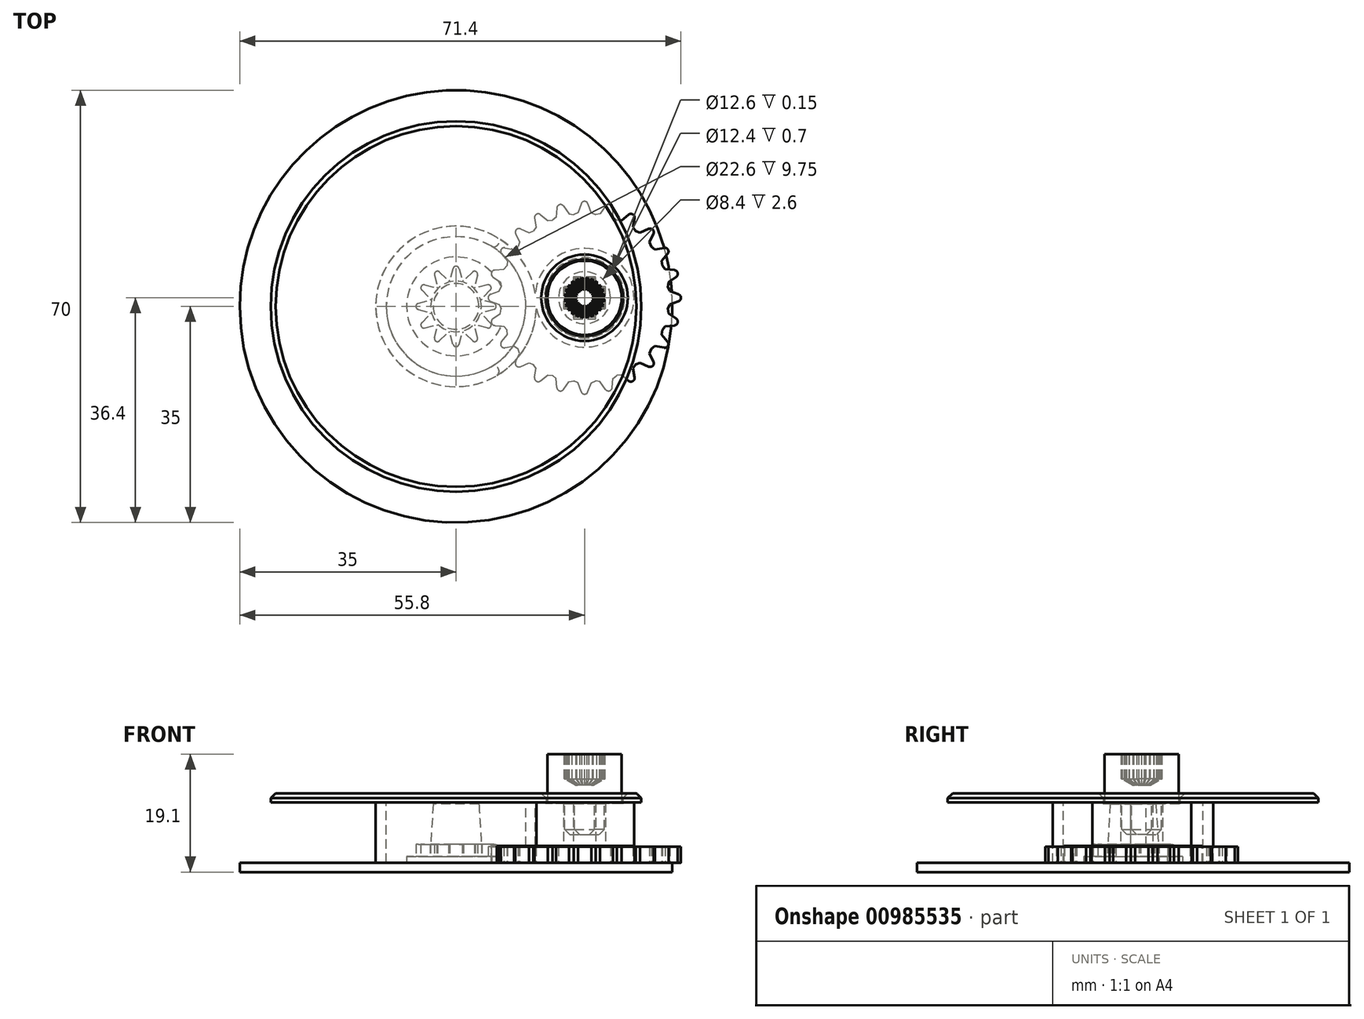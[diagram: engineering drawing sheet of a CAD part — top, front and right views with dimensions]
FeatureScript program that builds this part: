
annotation { "Feature Type Name" : "Feature", "Feature Type Description" : "" }
export const myFeature = defineFeature(function(context is Context, id is Id, definition is map)
    precondition{}
    {
        {
            var Q0;
            Q0=qCreatedBy(makeId("Front.planeOp"),FACE);
            var sketch = newSketch(context, id + "F0", { "sketchPlane" : qUnion([Q0])});
            skLineSegment(sketch, "E0", {"start": v(0, 0) * mm, "end": v(0, 9) * mm});
            skLineSegment(sketch, "E1", {"start": v(0, 9) * mm, "end": v(3.8, 9) * mm});
            skLineSegment(sketch, "E2", {"start": v(3.8, 9) * mm, "end": v(4.2, 2.5) * mm});
            skLineSegment(sketch, "E3", {"start": v(4.2, 2.5) * mm, "end": v(8, 2.5) * mm});
            skLineSegment(sketch, "E4", {"start": v(8, 2.5) * mm, "end": v(8, 1.5) * mm});
            skLineSegment(sketch, "E5", {"start": v(8, 1.5) * mm, "end": v(35, 1.5) * mm});
            skLineSegment(sketch, "E6", {"start": v(35, 1.5) * mm, "end": v(35, 0) * mm});
            skLineSegment(sketch, "E7", {"start": v(35, 0) * mm, "end": v(0, 0) * mm});
            skSolve(sketch);
        }
        {
            var Q0;
            Q0=qSketchRegion(id+"F0",true);
            var Q1;
            Q1=sQuery(id+"F0.wireOp",EDGE,"E0");
            revolve(context, id + "F1", {"surfaceOperationType" : NewSurfaceOperationType.NEW, "entities" : qUnion([Q0]), "axis" : qUnion([Q1]), "revolveType" : RevolveType.FULL});
        }
        {
            var Q0;
            Q0=qCreatedBy(makeId("Top.planeOp"),FACE);
            var sketch = newSketch(context, id + "F2", { "sketchPlane" : qUnion([Q0])});
            skCircle(sketch, "E8", {"center": v(0, 0) * mm, "radius": 15 * mm});
            skSolve(sketch);
        }
        {
            var Q0;
            Q0 = qSketchRegion(id + "F2", true);
            extrude(context, id + "F3", {"entities" : qUnion([Q0]), "depth" : 1.5 * mm, "offsetDistance" : 25 * mm});
        }
        {
            var Q0;
            Q0=makeQuery(id+"F3.opExtrude","CAP_FACE",FACE,{"disambiguationData":[OSD([sQuery(id+"F2.wireOp",EDGE,"E8")])],"isStart":false});
            var sketch = newSketch(context, id + "F4", { "sketchPlane" : qUnion([Q0])});
            skCircle(sketch, "E9", {"center": v(6, 0) * mm, "radius": 0.5 * mm});
            skLineSegment(sketch, "E10", {"start": v(6.13, 0.48) * mm, "end": v(4.2, 1) * mm});
            skLineSegment(sketch, "E11", {"start": v(4.2, 1) * mm, "end": v(3.85, 2.04) * mm});
            skLineSegment(sketch, "E12.MirrorCS", {"start": v(6.13, -0.48) * mm, "end": v(4.2, -1) * mm});
            skLineSegment(sketch, "E13.MirrorCS", {"start": v(4.2, -1) * mm, "end": v(3.85, -2.04) * mm});
            skCircle(sketch, "E14.1.0", {"center": v(5.2, 3) * mm, "radius": 0.5 * mm});
            skLineSegment(sketch, "E14.1.1", {"start": v(3.13, 2.97) * mm, "end": v(2.31, 3.69) * mm});
            skLineSegment(sketch, "E14.1.2", {"start": v(5.55, 2.65) * mm, "end": v(4.14, 1.23) * mm});
            skLineSegment(sketch, "E14.1.3", {"start": v(4.14, 1.23) * mm, "end": v(4.35, 0.16) * mm});
            skLineSegment(sketch, "E14.1.4", {"start": v(5.07, 3.48) * mm, "end": v(3.13, 2.97) * mm});
            skCircle(sketch, "E14.2.0", {"center": v(3, 5.2) * mm, "radius": 0.5 * mm});
            skLineSegment(sketch, "E14.2.1", {"start": v(1.23, 4.14) * mm, "end": v(0.16, 4.35) * mm});
            skLineSegment(sketch, "E14.2.2", {"start": v(3.48, 5.07) * mm, "end": v(2.97, 3.13) * mm});
            skLineSegment(sketch, "E14.2.3", {"start": v(2.97, 3.13) * mm, "end": v(3.69, 2.31) * mm});
            skLineSegment(sketch, "E14.2.4", {"start": v(2.65, 5.55) * mm, "end": v(1.23, 4.14) * mm});
            skCircle(sketch, "E14.3.0", {"center": v(0, 6) * mm, "radius": 0.5 * mm});
            skLineSegment(sketch, "E14.3.1", {"start": v(-1, 4.2) * mm, "end": v(-2.04, 3.85) * mm});
            skLineSegment(sketch, "E14.3.2", {"start": v(0.48, 6.13) * mm, "end": v(1, 4.2) * mm});
            skLineSegment(sketch, "E14.3.3", {"start": v(1, 4.2) * mm, "end": v(2.04, 3.85) * mm});
            skLineSegment(sketch, "E14.3.4", {"start": v(-0.48, 6.13) * mm, "end": v(-1, 4.2) * mm});
            skCircle(sketch, "E14.4.0", {"center": v(-3, 5.2) * mm, "radius": 0.5 * mm});
            skLineSegment(sketch, "E14.4.1", {"start": v(-2.97, 3.13) * mm, "end": v(-3.69, 2.31) * mm});
            skLineSegment(sketch, "E14.4.2", {"start": v(-2.65, 5.55) * mm, "end": v(-1.23, 4.14) * mm});
            skLineSegment(sketch, "E14.4.3", {"start": v(-1.23, 4.14) * mm, "end": v(-0.16, 4.35) * mm});
            skLineSegment(sketch, "E14.4.4", {"start": v(-3.48, 5.07) * mm, "end": v(-2.97, 3.13) * mm});
            skCircle(sketch, "E14.5.0", {"center": v(-5.2, 3) * mm, "radius": 0.5 * mm});
            skLineSegment(sketch, "E14.5.1", {"start": v(-4.14, 1.23) * mm, "end": v(-4.35, 0.16) * mm});
            skLineSegment(sketch, "E14.5.2", {"start": v(-5.07, 3.48) * mm, "end": v(-3.13, 2.97) * mm});
            skLineSegment(sketch, "E14.5.3", {"start": v(-3.13, 2.97) * mm, "end": v(-2.31, 3.69) * mm});
            skLineSegment(sketch, "E14.5.4", {"start": v(-5.55, 2.65) * mm, "end": v(-4.14, 1.23) * mm});
            skCircle(sketch, "E14.6.0", {"center": v(-6, 0) * mm, "radius": 0.5 * mm});
            skLineSegment(sketch, "E14.6.1", {"start": v(-4.2, -1) * mm, "end": v(-3.85, -2.04) * mm});
            skLineSegment(sketch, "E14.6.2", {"start": v(-6.13, 0.48) * mm, "end": v(-4.2, 1) * mm});
            skLineSegment(sketch, "E14.6.3", {"start": v(-4.2, 1) * mm, "end": v(-3.85, 2.04) * mm});
            skLineSegment(sketch, "E14.6.4", {"start": v(-6.13, -0.48) * mm, "end": v(-4.2, -1) * mm});
            skCircle(sketch, "E14.7.0", {"center": v(-5.2, -3) * mm, "radius": 0.5 * mm});
            skLineSegment(sketch, "E14.7.1", {"start": v(-3.13, -2.97) * mm, "end": v(-2.31, -3.69) * mm});
            skLineSegment(sketch, "E14.7.2", {"start": v(-5.55, -2.65) * mm, "end": v(-4.14, -1.23) * mm});
            skLineSegment(sketch, "E14.7.3", {"start": v(-4.14, -1.23) * mm, "end": v(-4.35, -0.16) * mm});
            skLineSegment(sketch, "E14.7.4", {"start": v(-5.07, -3.48) * mm, "end": v(-3.13, -2.97) * mm});
            skCircle(sketch, "E14.8.0", {"center": v(-3, -5.2) * mm, "radius": 0.5 * mm});
            skLineSegment(sketch, "E14.8.1", {"start": v(-1.23, -4.14) * mm, "end": v(-0.16, -4.35) * mm});
            skLineSegment(sketch, "E14.8.2", {"start": v(-3.48, -5.07) * mm, "end": v(-2.97, -3.13) * mm});
            skLineSegment(sketch, "E14.8.3", {"start": v(-2.97, -3.13) * mm, "end": v(-3.69, -2.31) * mm});
            skLineSegment(sketch, "E14.8.4", {"start": v(-2.65, -5.55) * mm, "end": v(-1.23, -4.14) * mm});
            skCircle(sketch, "E14.9.0", {"center": v(0, -6) * mm, "radius": 0.5 * mm});
            skLineSegment(sketch, "E14.9.1", {"start": v(1, -4.2) * mm, "end": v(2.04, -3.85) * mm});
            skLineSegment(sketch, "E14.9.2", {"start": v(-0.48, -6.13) * mm, "end": v(-1, -4.2) * mm});
            skLineSegment(sketch, "E14.9.3", {"start": v(-1, -4.2) * mm, "end": v(-2.04, -3.85) * mm});
            skLineSegment(sketch, "E14.9.4", {"start": v(0.48, -6.13) * mm, "end": v(1, -4.2) * mm});
            skPoint(sketch, "E14.center", {"position": v(0, 0) * mm});
            skLineSegment(sketch, "E15.2.10.0", {"start": v(2.97, -3.13) * mm, "end": v(3.69, -2.31) * mm});
            skLineSegment(sketch, "E15.5.10.0", {"start": v(2.65, -5.55) * mm, "end": v(1.23, -4.14) * mm});
            skLineSegment(sketch, "E15.8.10.0", {"start": v(1.23, -4.14) * mm, "end": v(0.16, -4.35) * mm});
            skCircle(sketch, "E15.10.10.0", {"center": v(3, -5.2) * mm, "radius": 0.5 * mm});
            skLineSegment(sketch, "E15.11.10.0", {"start": v(3.48, -5.07) * mm, "end": v(2.97, -3.13) * mm});
            skLineSegment(sketch, "E15.2.11.0", {"start": v(4.14, -1.23) * mm, "end": v(4.35, -0.16) * mm});
            skLineSegment(sketch, "E15.5.11.0", {"start": v(5.07, -3.48) * mm, "end": v(3.13, -2.97) * mm});
            skLineSegment(sketch, "E15.8.11.0", {"start": v(3.13, -2.97) * mm, "end": v(2.31, -3.69) * mm});
            skCircle(sketch, "E15.10.11.0", {"center": v(5.2, -3) * mm, "radius": 0.5 * mm});
            skLineSegment(sketch, "E15.11.11.0", {"start": v(5.55, -2.65) * mm, "end": v(4.14, -1.23) * mm});
            skSolve(sketch);
        }
        {
            var Q0;
            Q0=qSketchRegion(id+"F4",true);
            extrude(context, id + "F5", {"entities" : qUnion([Q0]), "operationType" : NewBodyOperationType.ADD, "depth" : 3 * mm, "offsetDistance" : 25 * mm});
        }
        {
            var Q0;
            Q0=makeQuery(id+"F1.opRevolve","SWEPT_FACE",FACE,{"disambiguationData":[OSD([sQuery(id+"F0.wireOp",EDGE,"E5")])]});
            var sketch = newSketch(context, id + "F6", { "sketchPlane" : qUnion([Q0])});
            skCircle(sketch, "E16", {"center": v(20.8, 1.4) * mm, "radius": 4.2 * mm});
            skCircle(sketch, "E17", {"center": v(35.8, 1.4) * mm, "radius": 0.6 * mm});
            skLineSegment(sketch, "E18", {"start": v(36, 1.96) * mm, "end": v(34.6, 2.48) * mm});
            skLineSegment(sketch, "E19", {"start": v(35.8, 1.4) * mm, "end": v(35.3, 1.4) * mm});
            skLineSegment(sketch, "E20", {"start": v(34.6, 2.48) * mm, "end": v(34.2, 3.4) * mm});
            skLineSegment(sketch, "E21.MirrorCS", {"start": v(36, 0.84) * mm, "end": v(34.6, 0.32) * mm});
            skLineSegment(sketch, "E22.MirrorCS", {"start": v(34.6, 0.32) * mm, "end": v(34.2, -0.6) * mm});
            skLineSegment(sketch, "E23.1.0", {"start": v(35.63, 4.8) * mm, "end": v(34.4, 3.93) * mm});
            skCircle(sketch, "E23.1.1", {"center": v(35.29, 5.28) * mm, "radius": 0.6 * mm});
            skLineSegment(sketch, "E23.1.2", {"start": v(35.34, 5.88) * mm, "end": v(33.85, 6.01) * mm});
            skLineSegment(sketch, "E23.1.3", {"start": v(34.4, 3.93) * mm, "end": v(34.25, 2.94) * mm});
            skLineSegment(sketch, "E23.1.4", {"start": v(33.85, 6.01) * mm, "end": v(33.22, 6.8) * mm});
            skLineSegment(sketch, "E23.1.5", {"start": v(35.29, 5.28) * mm, "end": v(34.8, 5.15) * mm});
            skLineSegment(sketch, "E23.2.0", {"start": v(34.25, 8.51) * mm, "end": v(33.29, 7.37) * mm});
            skCircle(sketch, "E23.2.1", {"center": v(33.8, 8.9) * mm, "radius": 0.6 * mm});
            skLineSegment(sketch, "E23.2.2", {"start": v(33.69, 9.5) * mm, "end": v(32.2, 9.23) * mm});
            skLineSegment(sketch, "E23.2.3", {"start": v(33.29, 7.37) * mm, "end": v(33.4, 6.37) * mm});
            skLineSegment(sketch, "E23.2.4", {"start": v(32.2, 9.23) * mm, "end": v(31.4, 9.82) * mm});
            skLineSegment(sketch, "E23.2.5", {"start": v(33.8, 8.9) * mm, "end": v(33.36, 8.65) * mm});
            skLineSegment(sketch, "E23.3.0", {"start": v(31.95, 11.75) * mm, "end": v(31.32, 10.4) * mm});
            skCircle(sketch, "E23.3.1", {"center": v(31.4, 12) * mm, "radius": 0.6 * mm});
            skLineSegment(sketch, "E23.3.2", {"start": v(31.15, 12.55) * mm, "end": v(29.8, 11.92) * mm});
            skLineSegment(sketch, "E23.3.3", {"start": v(31.32, 10.4) * mm, "end": v(31.68, 9.46) * mm});
            skLineSegment(sketch, "E23.3.4", {"start": v(29.8, 11.92) * mm, "end": v(28.86, 12.28) * mm});
            skLineSegment(sketch, "E23.3.5", {"start": v(31.4, 12) * mm, "end": v(31.05, 11.65) * mm});
            skLineSegment(sketch, "E23.4.0", {"start": v(28.9, 14.29) * mm, "end": v(28.63, 12.8) * mm});
            skCircle(sketch, "E23.4.1", {"center": v(28.3, 14.4) * mm, "radius": 0.6 * mm});
            skLineSegment(sketch, "E23.4.2", {"start": v(27.91, 14.85) * mm, "end": v(26.77, 13.89) * mm});
            skLineSegment(sketch, "E23.4.3", {"start": v(28.63, 12.8) * mm, "end": v(29.22, 12) * mm});
            skLineSegment(sketch, "E23.4.4", {"start": v(26.77, 13.89) * mm, "end": v(25.77, 14) * mm});
            skLineSegment(sketch, "E23.4.5", {"start": v(28.3, 14.4) * mm, "end": v(28.05, 13.96) * mm});
            skLineSegment(sketch, "E23.5.0", {"start": v(25.28, 15.94) * mm, "end": v(25.41, 14.45) * mm});
            skCircle(sketch, "E23.5.1", {"center": v(24.68, 15.89) * mm, "radius": 0.6 * mm});
            skLineSegment(sketch, "E23.5.2", {"start": v(24.2, 16.23) * mm, "end": v(23.33, 15) * mm});
            skLineSegment(sketch, "E23.5.3", {"start": v(25.41, 14.45) * mm, "end": v(26.2, 13.82) * mm});
            skLineSegment(sketch, "E23.5.4", {"start": v(23.33, 15) * mm, "end": v(22.34, 14.85) * mm});
            skLineSegment(sketch, "E23.5.5", {"start": v(24.68, 15.89) * mm, "end": v(24.55, 15.4) * mm});
            skLineSegment(sketch, "E23.6.0", {"start": v(21.36, 16.6) * mm, "end": v(21.88, 15.2) * mm});
            skCircle(sketch, "E23.6.1", {"center": v(20.8, 16.4) * mm, "radius": 0.6 * mm});
            skLineSegment(sketch, "E23.6.2", {"start": v(20.24, 16.6) * mm, "end": v(19.72, 15.2) * mm});
            skLineSegment(sketch, "E23.6.3", {"start": v(21.88, 15.2) * mm, "end": v(22.8, 14.8) * mm});
            skLineSegment(sketch, "E23.6.4", {"start": v(19.72, 15.2) * mm, "end": v(18.8, 14.8) * mm});
            skLineSegment(sketch, "E23.6.5", {"start": v(20.8, 16.4) * mm, "end": v(20.8, 15.9) * mm});
            skLineSegment(sketch, "E23.7.0", {"start": v(17.4, 16.23) * mm, "end": v(18.27, 15) * mm});
            skCircle(sketch, "E23.7.1", {"center": v(16.92, 15.89) * mm, "radius": 0.6 * mm});
            skLineSegment(sketch, "E23.7.2", {"start": v(16.32, 15.94) * mm, "end": v(16.19, 14.45) * mm});
            skLineSegment(sketch, "E23.7.3", {"start": v(18.27, 15) * mm, "end": v(19.26, 14.85) * mm});
            skLineSegment(sketch, "E23.7.4", {"start": v(16.19, 14.45) * mm, "end": v(15.4, 13.82) * mm});
            skLineSegment(sketch, "E23.7.5", {"start": v(16.92, 15.89) * mm, "end": v(17.05, 15.4) * mm});
            skLineSegment(sketch, "E23.8.0", {"start": v(13.69, 14.85) * mm, "end": v(14.83, 13.89) * mm});
            skCircle(sketch, "E23.8.1", {"center": v(13.3, 14.4) * mm, "radius": 0.6 * mm});
            skLineSegment(sketch, "E23.8.2", {"start": v(12.7, 14.29) * mm, "end": v(12.97, 12.8) * mm});
            skLineSegment(sketch, "E23.8.3", {"start": v(14.83, 13.89) * mm, "end": v(15.83, 14) * mm});
            skLineSegment(sketch, "E23.8.4", {"start": v(12.97, 12.8) * mm, "end": v(12.38, 12) * mm});
            skLineSegment(sketch, "E23.8.5", {"start": v(13.3, 14.4) * mm, "end": v(13.55, 13.96) * mm});
            skLineSegment(sketch, "E23.9.0", {"start": v(10.45, 12.55) * mm, "end": v(11.8, 11.92) * mm});
            skCircle(sketch, "E23.9.1", {"center": v(10.2, 12) * mm, "radius": 0.6 * mm});
            skLineSegment(sketch, "E23.9.2", {"start": v(9.65, 11.75) * mm, "end": v(10.28, 10.4) * mm});
            skLineSegment(sketch, "E23.9.3", {"start": v(11.8, 11.92) * mm, "end": v(12.74, 12.28) * mm});
            skLineSegment(sketch, "E23.9.4", {"start": v(10.28, 10.4) * mm, "end": v(9.92, 9.46) * mm});
            skLineSegment(sketch, "E23.9.5", {"start": v(10.2, 12) * mm, "end": v(10.55, 11.65) * mm});
            skLineSegment(sketch, "E23.10.0", {"start": v(7.91, 9.5) * mm, "end": v(9.4, 9.23) * mm});
            skCircle(sketch, "E23.10.1", {"center": v(7.8, 8.9) * mm, "radius": 0.6 * mm});
            skLineSegment(sketch, "E23.10.2", {"start": v(7.35, 8.51) * mm, "end": v(8.31, 7.37) * mm});
            skLineSegment(sketch, "E23.10.3", {"start": v(9.4, 9.23) * mm, "end": v(10.2, 9.82) * mm});
            skLineSegment(sketch, "E23.10.4", {"start": v(8.31, 7.37) * mm, "end": v(8.2, 6.37) * mm});
            skLineSegment(sketch, "E23.10.5", {"start": v(7.8, 8.9) * mm, "end": v(8.24, 8.65) * mm});
            skLineSegment(sketch, "E23.11.0", {"start": v(6.26, 5.88) * mm, "end": v(7.75, 6.01) * mm});
            skCircle(sketch, "E23.11.1", {"center": v(6.31, 5.28) * mm, "radius": 0.6 * mm});
            skLineSegment(sketch, "E23.11.2", {"start": v(5.97, 4.8) * mm, "end": v(7.2, 3.93) * mm});
            skLineSegment(sketch, "E23.11.3", {"start": v(7.75, 6.01) * mm, "end": v(8.38, 6.8) * mm});
            skLineSegment(sketch, "E23.11.4", {"start": v(7.2, 3.93) * mm, "end": v(7.35, 2.94) * mm});
            skLineSegment(sketch, "E23.11.5", {"start": v(6.31, 5.28) * mm, "end": v(6.8, 5.15) * mm});
            skLineSegment(sketch, "E23.12.0", {"start": v(5.6, 1.96) * mm, "end": v(7, 2.48) * mm});
            skCircle(sketch, "E23.12.1", {"center": v(5.8, 1.4) * mm, "radius": 0.6 * mm});
            skLineSegment(sketch, "E23.12.2", {"start": v(5.6, 0.84) * mm, "end": v(7, 0.32) * mm});
            skLineSegment(sketch, "E23.12.3", {"start": v(7, 2.48) * mm, "end": v(7.4, 3.4) * mm});
            skLineSegment(sketch, "E23.12.4", {"start": v(7, 0.32) * mm, "end": v(7.4, -0.6) * mm});
            skLineSegment(sketch, "E23.12.5", {"start": v(5.8, 1.4) * mm, "end": v(6.3, 1.4) * mm});
            skLineSegment(sketch, "E23.13.0", {"start": v(5.97, -2) * mm, "end": v(7.2, -1.13) * mm});
            skCircle(sketch, "E23.13.1", {"center": v(6.31, -2.48) * mm, "radius": 0.6 * mm});
            skLineSegment(sketch, "E23.13.2", {"start": v(6.26, -3.08) * mm, "end": v(7.75, -3.21) * mm});
            skLineSegment(sketch, "E23.13.3", {"start": v(7.2, -1.13) * mm, "end": v(7.35, -0.14) * mm});
            skLineSegment(sketch, "E23.13.4", {"start": v(7.75, -3.21) * mm, "end": v(8.38, -4) * mm});
            skLineSegment(sketch, "E23.13.5", {"start": v(6.31, -2.48) * mm, "end": v(6.8, -2.35) * mm});
            skLineSegment(sketch, "E23.14.0", {"start": v(7.35, -5.71) * mm, "end": v(8.31, -4.57) * mm});
            skCircle(sketch, "E23.14.1", {"center": v(7.8, -6.1) * mm, "radius": 0.6 * mm});
            skLineSegment(sketch, "E23.14.2", {"start": v(7.91, -6.7) * mm, "end": v(9.4, -6.43) * mm});
            skLineSegment(sketch, "E23.14.3", {"start": v(8.31, -4.57) * mm, "end": v(8.2, -3.57) * mm});
            skLineSegment(sketch, "E23.14.4", {"start": v(9.4, -6.43) * mm, "end": v(10.2, -7.02) * mm});
            skLineSegment(sketch, "E23.14.5", {"start": v(7.8, -6.1) * mm, "end": v(8.24, -5.85) * mm});
            skLineSegment(sketch, "E23.15.0", {"start": v(9.65, -8.95) * mm, "end": v(10.28, -7.6) * mm});
            skCircle(sketch, "E23.15.1", {"center": v(10.2, -9.2) * mm, "radius": 0.6 * mm});
            skLineSegment(sketch, "E23.15.2", {"start": v(10.45, -9.75) * mm, "end": v(11.8, -9.12) * mm});
            skLineSegment(sketch, "E23.15.3", {"start": v(10.28, -7.6) * mm, "end": v(9.92, -6.66) * mm});
            skLineSegment(sketch, "E23.15.4", {"start": v(11.8, -9.12) * mm, "end": v(12.74, -9.48) * mm});
            skLineSegment(sketch, "E23.15.5", {"start": v(10.2, -9.2) * mm, "end": v(10.55, -8.85) * mm});
            skLineSegment(sketch, "E23.16.0", {"start": v(12.7, -11.49) * mm, "end": v(12.97, -10) * mm});
            skCircle(sketch, "E23.16.1", {"center": v(13.3, -11.6) * mm, "radius": 0.6 * mm});
            skLineSegment(sketch, "E23.16.2", {"start": v(13.69, -12.05) * mm, "end": v(14.83, -11.09) * mm});
            skLineSegment(sketch, "E23.16.3", {"start": v(12.97, -10) * mm, "end": v(12.38, -9.2) * mm});
            skLineSegment(sketch, "E23.16.4", {"start": v(14.83, -11.09) * mm, "end": v(15.83, -11.2) * mm});
            skLineSegment(sketch, "E23.16.5", {"start": v(13.3, -11.6) * mm, "end": v(13.55, -11.16) * mm});
            skLineSegment(sketch, "E23.17.0", {"start": v(16.32, -13.14) * mm, "end": v(16.19, -11.65) * mm});
            skCircle(sketch, "E23.17.1", {"center": v(16.92, -13.09) * mm, "radius": 0.6 * mm});
            skLineSegment(sketch, "E23.17.2", {"start": v(17.4, -13.43) * mm, "end": v(18.27, -12.2) * mm});
            skLineSegment(sketch, "E23.17.3", {"start": v(16.19, -11.65) * mm, "end": v(15.4, -11.02) * mm});
            skLineSegment(sketch, "E23.17.4", {"start": v(18.27, -12.2) * mm, "end": v(19.26, -12.05) * mm});
            skLineSegment(sketch, "E23.17.5", {"start": v(16.92, -13.09) * mm, "end": v(17.05, -12.6) * mm});
            skLineSegment(sketch, "E23.18.0", {"start": v(20.24, -13.8) * mm, "end": v(19.72, -12.4) * mm});
            skCircle(sketch, "E23.18.1", {"center": v(20.8, -13.6) * mm, "radius": 0.6 * mm});
            skLineSegment(sketch, "E23.18.2", {"start": v(21.36, -13.8) * mm, "end": v(21.88, -12.4) * mm});
            skLineSegment(sketch, "E23.18.3", {"start": v(19.72, -12.4) * mm, "end": v(18.8, -12) * mm});
            skLineSegment(sketch, "E23.18.4", {"start": v(21.88, -12.4) * mm, "end": v(22.8, -12) * mm});
            skLineSegment(sketch, "E23.18.5", {"start": v(20.8, -13.6) * mm, "end": v(20.8, -13.1) * mm});
            skLineSegment(sketch, "E23.19.0", {"start": v(24.2, -13.43) * mm, "end": v(23.33, -12.2) * mm});
            skCircle(sketch, "E23.19.1", {"center": v(24.68, -13.09) * mm, "radius": 0.6 * mm});
            skLineSegment(sketch, "E23.19.2", {"start": v(25.28, -13.14) * mm, "end": v(25.41, -11.65) * mm});
            skLineSegment(sketch, "E23.19.3", {"start": v(23.33, -12.2) * mm, "end": v(22.34, -12.05) * mm});
            skLineSegment(sketch, "E23.19.4", {"start": v(25.41, -11.65) * mm, "end": v(26.2, -11.02) * mm});
            skLineSegment(sketch, "E23.19.5", {"start": v(24.68, -13.09) * mm, "end": v(24.55, -12.6) * mm});
            skLineSegment(sketch, "E23.20.0", {"start": v(27.91, -12.05) * mm, "end": v(26.77, -11.09) * mm});
            skCircle(sketch, "E23.20.1", {"center": v(28.3, -11.6) * mm, "radius": 0.6 * mm});
            skLineSegment(sketch, "E23.20.2", {"start": v(28.9, -11.49) * mm, "end": v(28.63, -10) * mm});
            skLineSegment(sketch, "E23.20.3", {"start": v(26.77, -11.09) * mm, "end": v(25.77, -11.2) * mm});
            skLineSegment(sketch, "E23.20.4", {"start": v(28.63, -10) * mm, "end": v(29.22, -9.2) * mm});
            skLineSegment(sketch, "E23.20.5", {"start": v(28.3, -11.6) * mm, "end": v(28.05, -11.16) * mm});
            skLineSegment(sketch, "E23.21.0", {"start": v(31.15, -9.75) * mm, "end": v(29.8, -9.12) * mm});
            skCircle(sketch, "E23.21.1", {"center": v(31.4, -9.2) * mm, "radius": 0.6 * mm});
            skLineSegment(sketch, "E23.21.2", {"start": v(31.95, -8.95) * mm, "end": v(31.32, -7.6) * mm});
            skLineSegment(sketch, "E23.21.3", {"start": v(29.8, -9.12) * mm, "end": v(28.86, -9.48) * mm});
            skLineSegment(sketch, "E23.21.4", {"start": v(31.32, -7.6) * mm, "end": v(31.68, -6.66) * mm});
            skLineSegment(sketch, "E23.21.5", {"start": v(31.4, -9.2) * mm, "end": v(31.05, -8.85) * mm});
            skLineSegment(sketch, "E23.22.0", {"start": v(33.69, -6.7) * mm, "end": v(32.2, -6.43) * mm});
            skCircle(sketch, "E23.22.1", {"center": v(33.8, -6.1) * mm, "radius": 0.6 * mm});
            skLineSegment(sketch, "E23.22.2", {"start": v(34.25, -5.71) * mm, "end": v(33.29, -4.57) * mm});
            skLineSegment(sketch, "E23.22.3", {"start": v(32.2, -6.43) * mm, "end": v(31.4, -7.02) * mm});
            skLineSegment(sketch, "E23.22.4", {"start": v(33.29, -4.57) * mm, "end": v(33.4, -3.57) * mm});
            skLineSegment(sketch, "E23.22.5", {"start": v(33.8, -6.1) * mm, "end": v(33.36, -5.85) * mm});
            skLineSegment(sketch, "E23.23.0", {"start": v(35.34, -3.08) * mm, "end": v(33.85, -3.21) * mm});
            skCircle(sketch, "E23.23.1", {"center": v(35.29, -2.48) * mm, "radius": 0.6 * mm});
            skLineSegment(sketch, "E23.23.2", {"start": v(35.63, -2) * mm, "end": v(34.4, -1.13) * mm});
            skLineSegment(sketch, "E23.23.3", {"start": v(33.85, -3.21) * mm, "end": v(33.22, -4) * mm});
            skLineSegment(sketch, "E23.23.4", {"start": v(34.4, -1.13) * mm, "end": v(34.25, -0.14) * mm});
            skLineSegment(sketch, "E23.23.5", {"start": v(35.29, -2.48) * mm, "end": v(34.8, -2.35) * mm});
            skSolve(sketch);
        }
        {
            var Q0;
            Q0 = qSketchRegion(id + "F6", true);
            extrude(context, id + "F7", {"entities" : qUnion([Q0]), "depth" : 2.6 * mm, "offsetDistance" : 25 * mm});
        }
        {
            var Q0;
            Q0=makeQuery(id+"F5.opExtrude","CAP_FACE",FACE,{"disambiguationData":[OSD([sQuery(id+"F4.wireOp",EDGE,"0EXkI3EO-WUdj-fHIo-xL43-ZjD347GY3SOE"),sQuery(id+"F4.wireOp",EDGE,"E9"),sQuery(id+"F4.wireOp",EDGE,"E10"),sQuery(id+"F4.wireOp",EDGE,"E11"),sQuery(id+"F4.wireOp",EDGE,"E12.MirrorCS"),sQuery(id+"F4.wireOp",EDGE,"E13.MirrorCS"),sQuery(id+"F4.wireOp",EDGE,"E14.1.0"),sQuery(id+"F4.wireOp",EDGE,"E14.1.1"),sQuery(id+"F4.wireOp",EDGE,"E14.1.2"),sQuery(id+"F4.wireOp",EDGE,"E14.1.3"),sQuery(id+"F4.wireOp",EDGE,"E14.1.4"),sQuery(id+"F4.wireOp",EDGE,"E14.2.0"),sQuery(id+"F4.wireOp",EDGE,"E14.2.1"),sQuery(id+"F4.wireOp",EDGE,"E14.2.2"),sQuery(id+"F4.wireOp",EDGE,"E14.2.3"),sQuery(id+"F4.wireOp",EDGE,"E14.2.4"),sQuery(id+"F4.wireOp",EDGE,"E14.3.0"),sQuery(id+"F4.wireOp",EDGE,"E14.3.1"),sQuery(id+"F4.wireOp",EDGE,"E14.3.2"),sQuery(id+"F4.wireOp",EDGE,"E14.3.3"),sQuery(id+"F4.wireOp",EDGE,"E14.3.4"),sQuery(id+"F4.wireOp",EDGE,"E14.4.0"),sQuery(id+"F4.wireOp",EDGE,"E14.4.1"),sQuery(id+"F4.wireOp",EDGE,"E14.4.2"),sQuery(id+"F4.wireOp",EDGE,"E14.4.3"),sQuery(id+"F4.wireOp",EDGE,"E14.4.4"),sQuery(id+"F4.wireOp",EDGE,"E14.5.0"),sQuery(id+"F4.wireOp",EDGE,"E14.5.1"),sQuery(id+"F4.wireOp",EDGE,"E14.5.2"),sQuery(id+"F4.wireOp",EDGE,"E14.5.3"),sQuery(id+"F4.wireOp",EDGE,"E14.5.4"),sQuery(id+"F4.wireOp",EDGE,"E14.6.0"),sQuery(id+"F4.wireOp",EDGE,"E14.6.1"),sQuery(id+"F4.wireOp",EDGE,"E14.6.2"),sQuery(id+"F4.wireOp",EDGE,"E14.6.3"),sQuery(id+"F4.wireOp",EDGE,"E14.6.4"),sQuery(id+"F4.wireOp",EDGE,"E14.7.0"),sQuery(id+"F4.wireOp",EDGE,"E14.7.1"),sQuery(id+"F4.wireOp",EDGE,"E14.7.2"),sQuery(id+"F4.wireOp",EDGE,"E14.7.3"),sQuery(id+"F4.wireOp",EDGE,"E14.7.4"),sQuery(id+"F4.wireOp",EDGE,"E14.8.0"),sQuery(id+"F4.wireOp",EDGE,"E14.8.1"),sQuery(id+"F4.wireOp",EDGE,"E14.8.2"),sQuery(id+"F4.wireOp",EDGE,"E14.8.3"),sQuery(id+"F4.wireOp",EDGE,"E14.8.4"),sQuery(id+"F4.wireOp",EDGE,"E14.9.0"),sQuery(id+"F4.wireOp",EDGE,"E14.9.1"),sQuery(id+"F4.wireOp",EDGE,"E14.9.2"),sQuery(id+"F4.wireOp",EDGE,"E14.9.3"),sQuery(id+"F4.wireOp",EDGE,"E14.9.4"),sQuery(id+"F4.wireOp",EDGE,"E15.2.10.0"),sQuery(id+"F4.wireOp",EDGE,"E15.5.10.0"),sQuery(id+"F4.wireOp",EDGE,"E15.8.10.0"),sQuery(id+"F4.wireOp",EDGE,"E15.10.10.0"),sQuery(id+"F4.wireOp",EDGE,"E15.11.10.0"),sQuery(id+"F4.wireOp",EDGE,"E15.2.11.0"),sQuery(id+"F4.wireOp",EDGE,"E15.5.11.0"),sQuery(id+"F4.wireOp",EDGE,"E15.8.11.0"),sQuery(id+"F4.wireOp",EDGE,"E15.10.11.0"),sQuery(id+"F4.wireOp",EDGE,"E15.11.11.0")])],"isStart":false});
            var sketch = newSketch(context, id + "F8", { "sketchPlane" : qUnion([Q0])});
            skSolve(sketch);
        }
        {
            var Q0;
            Q0=makeQuery(id+"F8.imprint","IMPRINT",FACE,{"disambiguationData":[TD([[makeQuery(id+"F8.imprint","IMPRINT",EDGE,{"derivedFrom":makeQuery(id+"F5.opExtrude","CAP_EDGE",EDGE,{"disambiguationData":[OSD([sQuery(id+"F4.wireOp",EDGE,"E9")])],"isStart":false})}),1.0]])]});
            var sketch = newSketch(context, id + "F9", { "sketchPlane" : qUnion([Q0])});
            skCircle(sketch, "E24", {"center": v(0, 0) * mm, "radius": 4.1 * mm});
            skSolve(sketch);
        }
        {
            var Q0;
            Q0 = qSketchRegion(id + "F9", true);
            extrude(context, id + "F10", {"entities" : qUnion([Q0]), "operationType" : NewBodyOperationType.ADD, "depth" : 6.5 * mm, "offsetDistance" : 25 * mm});
        }
        {
            var Q0;
            Q0=makeQuery(id+"F10.opExtrude","CAP_EDGE",EDGE,{"disambiguationData":[OSD([sQuery(id+"F9.wireOp",EDGE,"E24")])],"isStart":false});
            chamfer(context, id + "F11", {"entities" : qUnion([Q0]), "chamferType" : ChamferType.TWO_OFFSETS, "width1" : .4 * mm, "oppositeDirection" : false, "width2" : 6.5 * mm, "tangentPropagation" : true});
        }
        {
            var Q0;
            Q0=makeQuery(id+"F10.opExtrude","CAP_FACE",FACE,{"disambiguationData":[OSD([sQuery(id+"F9.wireOp",EDGE,"E24")])],"isStart":false});
            cPlane(context, id + "F12", {"entities" : qUnion([Q0]), "cplaneType" : CPlaneType.OFFSET, "offset" : .25 * mm, "width" : 150 * mm, "height" : 150 * mm});
        }
        {
            var Q0;
            Q0=qCreatedBy(id+"F12.planeOp",FACE);
            var sketch = newSketch(context, id + "F13", { "sketchPlane" : qUnion([Q0])});
            skCircle(sketch, "E25", {"center": v(0, 0) * mm, "radius": 30 * mm});
            skCircle(sketch, "E26", {"center": v(20.8, 1.4) * mm, "radius": 6.2 * mm});
            skSolve(sketch);
        }
        {
            var Q0;
            Q0 = qSketchRegion(id + "F13", true);
            extrude(context, id + "F14", {"entities" : qUnion([Q0]), "depth" : 1.5 * mm, "offsetDistance" : 25 * mm});
        }
        {
            var Q0;
            Q0=makeQuery(id+"F14.opExtrude","CAP_FACE",FACE,{"disambiguationData":[OSD([sQuery(id+"F13.wireOp",EDGE,"E25")])],"isStart":true});
            var sketch = newSketch(context, id + "F15", { "sketchPlane" : qUnion([Q0])});
            skCircle(sketch, "E27", {"center": v(0, 0) * mm, "radius": 11.3 * mm});
            skCircle(sketch, "E28", {"center": v(0, 0) * mm, "radius": 13 * mm});
            skCircle(sketch, "E29", {"center": v(20.8, -1.4) * mm, "radius": 6.3 * mm});
            skCircle(sketch, "E30", {"center": v(20.8, -1.4) * mm, "radius": 8 * mm});
            skSolve(sketch);
        }
        {
            var Q0;
            Q0 = qSketchRegion(id + "F15", true);
            extrude(context, id + "F16", {"entities" : qUnion([Q0]), "operationType" : NewBodyOperationType.ADD, "depth" : 7 * mm, "offsetDistance" : 25 * mm});
        }
        {
            var Q0;
            Q0=makeQuery(id+"F7.opExtrude","CAP_FACE",FACE,{"disambiguationData":[OSD([sQuery(id+"F6.wireOp",EDGE,"E16"),sQuery(id+"F6.wireOp",EDGE,"E17"),sQuery(id+"F6.wireOp",EDGE,"E18"),sQuery(id+"F6.wireOp",EDGE,"E20"),sQuery(id+"F6.wireOp",EDGE,"E21.MirrorCS"),sQuery(id+"F6.wireOp",EDGE,"E22.MirrorCS"),sQuery(id+"F6.wireOp",EDGE,"E23.1.0"),sQuery(id+"F6.wireOp",EDGE,"E23.1.1"),sQuery(id+"F6.wireOp",EDGE,"E23.1.2"),sQuery(id+"F6.wireOp",EDGE,"E23.1.3"),sQuery(id+"F6.wireOp",EDGE,"E23.1.4"),sQuery(id+"F6.wireOp",EDGE,"E23.2.0"),sQuery(id+"F6.wireOp",EDGE,"E23.2.1"),sQuery(id+"F6.wireOp",EDGE,"E23.2.2"),sQuery(id+"F6.wireOp",EDGE,"E23.2.3"),sQuery(id+"F6.wireOp",EDGE,"E23.2.4"),sQuery(id+"F6.wireOp",EDGE,"E23.3.0"),sQuery(id+"F6.wireOp",EDGE,"E23.3.1"),sQuery(id+"F6.wireOp",EDGE,"E23.3.2"),sQuery(id+"F6.wireOp",EDGE,"E23.3.3"),sQuery(id+"F6.wireOp",EDGE,"E23.3.4"),sQuery(id+"F6.wireOp",EDGE,"E23.4.0"),sQuery(id+"F6.wireOp",EDGE,"E23.4.1"),sQuery(id+"F6.wireOp",EDGE,"E23.4.2"),sQuery(id+"F6.wireOp",EDGE,"E23.4.3"),sQuery(id+"F6.wireOp",EDGE,"E23.4.4"),sQuery(id+"F6.wireOp",EDGE,"E23.5.0"),sQuery(id+"F6.wireOp",EDGE,"E23.5.1"),sQuery(id+"F6.wireOp",EDGE,"E23.5.2"),sQuery(id+"F6.wireOp",EDGE,"E23.5.3"),sQuery(id+"F6.wireOp",EDGE,"E23.5.4"),sQuery(id+"F6.wireOp",EDGE,"E23.6.0"),sQuery(id+"F6.wireOp",EDGE,"E23.6.1"),sQuery(id+"F6.wireOp",EDGE,"E23.6.2"),sQuery(id+"F6.wireOp",EDGE,"E23.6.3"),sQuery(id+"F6.wireOp",EDGE,"E23.6.4"),sQuery(id+"F6.wireOp",EDGE,"E23.7.0"),sQuery(id+"F6.wireOp",EDGE,"E23.7.1"),sQuery(id+"F6.wireOp",EDGE,"E23.7.2"),sQuery(id+"F6.wireOp",EDGE,"E23.7.3"),sQuery(id+"F6.wireOp",EDGE,"E23.7.4"),sQuery(id+"F6.wireOp",EDGE,"E23.8.0"),sQuery(id+"F6.wireOp",EDGE,"E23.8.1"),sQuery(id+"F6.wireOp",EDGE,"E23.8.2"),sQuery(id+"F6.wireOp",EDGE,"E23.8.3"),sQuery(id+"F6.wireOp",EDGE,"E23.8.4"),sQuery(id+"F6.wireOp",EDGE,"E23.9.0"),sQuery(id+"F6.wireOp",EDGE,"E23.9.1"),sQuery(id+"F6.wireOp",EDGE,"E23.9.2"),sQuery(id+"F6.wireOp",EDGE,"E23.9.3"),sQuery(id+"F6.wireOp",EDGE,"E23.9.4"),sQuery(id+"F6.wireOp",EDGE,"E23.10.0"),sQuery(id+"F6.wireOp",EDGE,"E23.10.1"),sQuery(id+"F6.wireOp",EDGE,"E23.10.2"),sQuery(id+"F6.wireOp",EDGE,"E23.10.3"),sQuery(id+"F6.wireOp",EDGE,"E23.10.4"),sQuery(id+"F6.wireOp",EDGE,"E23.11.0"),sQuery(id+"F6.wireOp",EDGE,"E23.11.1"),sQuery(id+"F6.wireOp",EDGE,"E23.11.2"),sQuery(id+"F6.wireOp",EDGE,"E23.11.3"),sQuery(id+"F6.wireOp",EDGE,"E23.11.4"),sQuery(id+"F6.wireOp",EDGE,"E23.12.0"),sQuery(id+"F6.wireOp",EDGE,"E23.12.1"),sQuery(id+"F6.wireOp",EDGE,"E23.12.2"),sQuery(id+"F6.wireOp",EDGE,"E23.12.3"),sQuery(id+"F6.wireOp",EDGE,"E23.12.4"),sQuery(id+"F6.wireOp",EDGE,"E23.13.0"),sQuery(id+"F6.wireOp",EDGE,"E23.13.1"),sQuery(id+"F6.wireOp",EDGE,"E23.13.2"),sQuery(id+"F6.wireOp",EDGE,"E23.13.3"),sQuery(id+"F6.wireOp",EDGE,"E23.13.4"),sQuery(id+"F6.wireOp",EDGE,"E23.14.0"),sQuery(id+"F6.wireOp",EDGE,"E23.14.1"),sQuery(id+"F6.wireOp",EDGE,"E23.14.2"),sQuery(id+"F6.wireOp",EDGE,"E23.14.3"),sQuery(id+"F6.wireOp",EDGE,"E23.14.4"),sQuery(id+"F6.wireOp",EDGE,"E23.15.0"),sQuery(id+"F6.wireOp",EDGE,"E23.15.1"),sQuery(id+"F6.wireOp",EDGE,"E23.15.2"),sQuery(id+"F6.wireOp",EDGE,"E23.15.3"),sQuery(id+"F6.wireOp",EDGE,"E23.15.4"),sQuery(id+"F6.wireOp",EDGE,"E23.16.0"),sQuery(id+"F6.wireOp",EDGE,"E23.16.1"),sQuery(id+"F6.wireOp",EDGE,"E23.16.2"),sQuery(id+"F6.wireOp",EDGE,"E23.16.3"),sQuery(id+"F6.wireOp",EDGE,"E23.16.4"),sQuery(id+"F6.wireOp",EDGE,"E23.17.0"),sQuery(id+"F6.wireOp",EDGE,"E23.17.1"),sQuery(id+"F6.wireOp",EDGE,"E23.17.2"),sQuery(id+"F6.wireOp",EDGE,"E23.17.3"),sQuery(id+"F6.wireOp",EDGE,"E23.17.4"),sQuery(id+"F6.wireOp",EDGE,"E23.18.0"),sQuery(id+"F6.wireOp",EDGE,"E23.18.1"),sQuery(id+"F6.wireOp",EDGE,"E23.18.2"),sQuery(id+"F6.wireOp",EDGE,"E23.18.3"),sQuery(id+"F6.wireOp",EDGE,"E23.18.4"),sQuery(id+"F6.wireOp",EDGE,"E23.19.0"),sQuery(id+"F6.wireOp",EDGE,"E23.19.1"),sQuery(id+"F6.wireOp",EDGE,"E23.19.2"),sQuery(id+"F6.wireOp",EDGE,"E23.19.3"),sQuery(id+"F6.wireOp",EDGE,"E23.19.4"),sQuery(id+"F6.wireOp",EDGE,"E23.20.0"),sQuery(id+"F6.wireOp",EDGE,"E23.20.1"),sQuery(id+"F6.wireOp",EDGE,"E23.20.2"),sQuery(id+"F6.wireOp",EDGE,"E23.20.3"),sQuery(id+"F6.wireOp",EDGE,"E23.20.4"),sQuery(id+"F6.wireOp",EDGE,"E23.21.0"),sQuery(id+"F6.wireOp",EDGE,"E23.21.1"),sQuery(id+"F6.wireOp",EDGE,"E23.21.2"),sQuery(id+"F6.wireOp",EDGE,"E23.21.3"),sQuery(id+"F6.wireOp",EDGE,"E23.21.4"),sQuery(id+"F6.wireOp",EDGE,"E23.22.0"),sQuery(id+"F6.wireOp",EDGE,"E23.22.1"),sQuery(id+"F6.wireOp",EDGE,"E23.22.2"),sQuery(id+"F6.wireOp",EDGE,"E23.22.3"),sQuery(id+"F6.wireOp",EDGE,"E23.22.4"),sQuery(id+"F6.wireOp",EDGE,"E23.23.0"),sQuery(id+"F6.wireOp",EDGE,"E23.23.1"),sQuery(id+"F6.wireOp",EDGE,"E23.23.2"),sQuery(id+"F6.wireOp",EDGE,"E23.23.3"),sQuery(id+"F6.wireOp",EDGE,"E23.23.4")])],"isStart":false});
            var sketch = newSketch(context, id + "F17", { "sketchPlane" : qUnion([Q0])});
            skCircle(sketch, "E31", {"center": v(20.8, 1.4) * mm, "radius": 6.5 * mm});
            skLineSegment(sketch, "E32", {"start": v(24.2, 1.4) * mm, "end": v(24.2, 3.2) * mm});
            skLineSegment(sketch, "E33", {"start": v(24.2, 3.2) * mm, "end": v(22.6, 3.2) * mm});
            skLineSegment(sketch, "E34", {"start": v(22.6, 3.2) * mm, "end": v(22.6, 4.8) * mm});
            skLineSegment(sketch, "E35", {"start": v(22.6, 4.8) * mm, "end": v(20.8, 4.8) * mm});
            skLineSegment(sketch, "E36", {"start": v(20.8, 4.8) * mm, "end": v(20.8, 1.4) * mm});
            skLineSegment(sketch, "E37", {"start": v(24.2, 1.4) * mm, "end": v(20.8, 1.4) * mm});
            skLineSegment(sketch, "E38.1.0", {"start": v(17.4, 1.4) * mm, "end": v(20.8, 1.4) * mm});
            skLineSegment(sketch, "E38.1.1", {"start": v(20.8, 4.8) * mm, "end": v(19, 4.8) * mm});
            skLineSegment(sketch, "E38.1.3", {"start": v(19, 4.8) * mm, "end": v(19, 3.2) * mm});
            skLineSegment(sketch, "E38.1.4", {"start": v(19, 3.2) * mm, "end": v(17.4, 3.2) * mm});
            skLineSegment(sketch, "E38.1.5", {"start": v(17.4, 3.2) * mm, "end": v(17.4, 1.4) * mm});
            skLineSegment(sketch, "E38.2.0", {"start": v(20.8, -2) * mm, "end": v(20.8, 1.4) * mm});
            skLineSegment(sketch, "E38.2.1", {"start": v(17.4, 1.4) * mm, "end": v(17.4, -0.4) * mm});
            skLineSegment(sketch, "E38.2.2", {"start": v(17.4, 1.4) * mm, "end": v(20.8, 1.4) * mm});
            skLineSegment(sketch, "E38.2.3", {"start": v(17.4, -0.4) * mm, "end": v(19, -0.4) * mm});
            skLineSegment(sketch, "E38.2.4", {"start": v(19, -0.4) * mm, "end": v(19, -2) * mm});
            skLineSegment(sketch, "E38.2.5", {"start": v(19, -2) * mm, "end": v(20.8, -2) * mm});
            skLineSegment(sketch, "E38.3.1", {"start": v(20.8, -2) * mm, "end": v(22.6, -2) * mm});
            skLineSegment(sketch, "E38.3.2", {"start": v(20.8, -2) * mm, "end": v(20.8, 1.4) * mm});
            skLineSegment(sketch, "E38.3.3", {"start": v(22.6, -2) * mm, "end": v(22.6, -0.4) * mm});
            skLineSegment(sketch, "E38.3.4", {"start": v(22.6, -0.4) * mm, "end": v(24.2, -0.4) * mm});
            skLineSegment(sketch, "E38.3.5", {"start": v(24.2, -0.4) * mm, "end": v(24.2, 1.4) * mm});
            skSolve(sketch);
        }
        {
            var Q0;
            Q0 = qSketchRegion(id + "F17", true);
            extrude(context, id + "F18", {"entities" : qUnion([Q0]), "operationType" : NewBodyOperationType.ADD, "depth" : 7 * mm, "offsetDistance" : 25 * mm});
        }
        {
            var Q0;
            Q0=makeQuery(id+"F18.opExtrude","CAP_FACE",FACE,{"disambiguationData":[OSD([sQuery(id+"F17.wireOp",EDGE,"E31"),sQuery(id+"F17.wireOp",EDGE,"E32"),sQuery(id+"F17.wireOp",EDGE,"E33"),sQuery(id+"F17.wireOp",EDGE,"E34"),sQuery(id+"F17.wireOp",EDGE,"E35"),sQuery(id+"F17.wireOp",EDGE,"E38.1.1"),sQuery(id+"F17.wireOp",EDGE,"E38.1.3"),sQuery(id+"F17.wireOp",EDGE,"E38.1.4"),sQuery(id+"F17.wireOp",EDGE,"E38.1.5"),sQuery(id+"F17.wireOp",EDGE,"E38.2.1"),sQuery(id+"F17.wireOp",EDGE,"E38.2.3"),sQuery(id+"F17.wireOp",EDGE,"E38.2.4"),sQuery(id+"F17.wireOp",EDGE,"E38.2.5"),sQuery(id+"F17.wireOp",EDGE,"E38.3.1"),sQuery(id+"F17.wireOp",EDGE,"E38.3.3"),sQuery(id+"F17.wireOp",EDGE,"E38.3.4"),sQuery(id+"F17.wireOp",EDGE,"E38.3.5")])],"isStart":false});
            var sketch = newSketch(context, id + "F19", { "sketchPlane" : qUnion([Q0])});
            skLineSegment(sketch, "E39", {"start": v(20.8, 1.4) * mm, "end": v(20.8, 4.6) * mm});
            skLineSegment(sketch, "E40", {"start": v(20.8, 4.6) * mm, "end": v(22.4, 4.6) * mm});
            skLineSegment(sketch, "E41", {"start": v(22.4, 4.6) * mm, "end": v(22.4, 3) * mm});
            skLineSegment(sketch, "E42", {"start": v(22.4, 3) * mm, "end": v(24, 3) * mm});
            skLineSegment(sketch, "E43", {"start": v(24, 3) * mm, "end": v(24, 1.4) * mm});
            skLineSegment(sketch, "E44", {"start": v(24, 1.4) * mm, "end": v(20.8, 1.4) * mm});
            skLineSegment(sketch, "E45.1.0", {"start": v(17.6, 1.4) * mm, "end": v(17.6, 3) * mm});
            skLineSegment(sketch, "E45.1.1", {"start": v(20.8, 4.6) * mm, "end": v(20.8, 1.4) * mm});
            skLineSegment(sketch, "E45.1.2", {"start": v(20.8, 1.4) * mm, "end": v(17.6, 1.4) * mm});
            skLineSegment(sketch, "E45.1.3", {"start": v(19.2, 3) * mm, "end": v(19.2, 4.6) * mm});
            skLineSegment(sketch, "E45.1.4", {"start": v(19.2, 4.6) * mm, "end": v(20.8, 4.6) * mm});
            skLineSegment(sketch, "E45.1.5", {"start": v(17.6, 3) * mm, "end": v(19.2, 3) * mm});
            skLineSegment(sketch, "E45.2.0", {"start": v(20.8, -1.8) * mm, "end": v(19.2, -1.8) * mm});
            skLineSegment(sketch, "E45.2.1", {"start": v(17.6, 1.4) * mm, "end": v(20.8, 1.4) * mm});
            skLineSegment(sketch, "E45.2.2", {"start": v(20.8, 1.4) * mm, "end": v(20.8, -1.8) * mm});
            skLineSegment(sketch, "E45.2.3", {"start": v(19.2, -0.2) * mm, "end": v(17.6, -0.2) * mm});
            skLineSegment(sketch, "E45.2.4", {"start": v(17.6, -0.2) * mm, "end": v(17.6, 1.4) * mm});
            skLineSegment(sketch, "E45.2.5", {"start": v(19.2, -1.8) * mm, "end": v(19.2, -0.2) * mm});
            skLineSegment(sketch, "E45.3.0", {"start": v(24, 1.4) * mm, "end": v(24, -0.2) * mm});
            skLineSegment(sketch, "E45.3.1", {"start": v(20.8, -1.8) * mm, "end": v(20.8, 1.4) * mm});
            skLineSegment(sketch, "E45.3.2", {"start": v(20.8, 1.4) * mm, "end": v(24, 1.4) * mm});
            skLineSegment(sketch, "E45.3.3", {"start": v(22.4, -0.2) * mm, "end": v(22.4, -1.8) * mm});
            skLineSegment(sketch, "E45.3.4", {"start": v(22.4, -1.8) * mm, "end": v(20.8, -1.8) * mm});
            skLineSegment(sketch, "E45.3.5", {"start": v(24, -0.2) * mm, "end": v(22.4, -0.2) * mm});
            skPoint(sketch, "E45.center", {"position": v(20.8, 1.4) * mm});
            skSolve(sketch);
        }
        {
            var Q0;
            Q0 = qSketchRegion(id + "F19", true);
            extrude(context, id + "F20", {"entities" : qUnion([Q0]), "oppositeDirection" : true, "depth" : 5 * mm, "offsetDistance" : 25 * mm});
        }
        {
            var Q0;
            Q0=makeQuery(id+"F20.opExtrude","CAP_FACE",FACE,{"disambiguationData":[OSD([sQuery(id+"F19.wireOp",EDGE,"E40"),sQuery(id+"F19.wireOp",EDGE,"E41"),sQuery(id+"F19.wireOp",EDGE,"E42"),sQuery(id+"F19.wireOp",EDGE,"E43"),sQuery(id+"F19.wireOp",EDGE,"E45.1.0"),sQuery(id+"F19.wireOp",EDGE,"E45.1.3"),sQuery(id+"F19.wireOp",EDGE,"E45.1.4"),sQuery(id+"F19.wireOp",EDGE,"E45.1.5"),sQuery(id+"F19.wireOp",EDGE,"E45.2.0"),sQuery(id+"F19.wireOp",EDGE,"E45.2.3"),sQuery(id+"F19.wireOp",EDGE,"E45.2.4"),sQuery(id+"F19.wireOp",EDGE,"E45.2.5"),sQuery(id+"F19.wireOp",EDGE,"E45.3.0"),sQuery(id+"F19.wireOp",EDGE,"E45.3.3"),sQuery(id+"F19.wireOp",EDGE,"E45.3.4"),sQuery(id+"F19.wireOp",EDGE,"E45.3.5")])],"isStart":true});
            var sketch = newSketch(context, id + "F21", { "sketchPlane" : qUnion([Q0])});
            skCircle(sketch, "E46", {"center": v(20.8, 1.4) * mm, "radius": 6 * mm});
            skPoint(sketch, "E46.centerSnap0", {"position": v(20.8, 4.6) * mm});
            skPoint(sketch, "E46.centerSnap1", {"position": v(17.6, 1.4) * mm});
            skSolve(sketch);
        }
        {
            var Q0;
            Q0 = qSketchRegion(id + "F21", true);
            extrude(context, id + "F22", {"entities" : qUnion([Q0]), "operationType" : NewBodyOperationType.ADD, "depth" : 8 * mm, "offsetDistance" : 25 * mm});
        }
        {
            var Q0;
            Q0=makeQuery(id+"F14.opExtrude","CAP_FACE",FACE,{"disambiguationData":[OSD([sQuery(id+"F13.wireOp",EDGE,"E25"),sQuery(id+"F13.wireOp",EDGE,"E26")])],"isStart":false});
            var Q1;
            Q1=makeQuery(id+"F20.opExtrude","CAP_FACE",FACE,{"disambiguationData":[OSD([sQuery(id+"F19.wireOp",EDGE,"E40"),sQuery(id+"F19.wireOp",EDGE,"E41"),sQuery(id+"F19.wireOp",EDGE,"E42"),sQuery(id+"F19.wireOp",EDGE,"E43"),sQuery(id+"F19.wireOp",EDGE,"E45.1.0"),sQuery(id+"F19.wireOp",EDGE,"E45.1.3"),sQuery(id+"F19.wireOp",EDGE,"E45.1.4"),sQuery(id+"F19.wireOp",EDGE,"E45.1.5"),sQuery(id+"F19.wireOp",EDGE,"E45.2.0"),sQuery(id+"F19.wireOp",EDGE,"E45.2.3"),sQuery(id+"F19.wireOp",EDGE,"E45.2.4"),sQuery(id+"F19.wireOp",EDGE,"E45.2.5"),sQuery(id+"F19.wireOp",EDGE,"E45.3.0"),sQuery(id+"F19.wireOp",EDGE,"E45.3.3"),sQuery(id+"F19.wireOp",EDGE,"E45.3.4"),sQuery(id+"F19.wireOp",EDGE,"E45.3.5")])],"isStart":false});
            var Q2;
            Q2=makeQuery(id+"F18.opExtrude","CAP_EDGE",EDGE,{"disambiguationData":[OSD([sQuery(id+"F17.wireOp",EDGE,"E32"),sQuery(id+"F17.wireOp",EDGE,"E38.3.5")])],"isStart":false});
            var Q3;
            Q3=makeQuery(id+"F18.opExtrude","CAP_EDGE",EDGE,{"disambiguationData":[OSD([sQuery(id+"F17.wireOp",EDGE,"E38.3.4")])],"isStart":false});
            var Q4;
            Q4=makeQuery(id+"F18.opExtrude","CAP_EDGE",EDGE,{"disambiguationData":[OSD([sQuery(id+"F17.wireOp",EDGE,"E38.2.5"),sQuery(id+"F17.wireOp",EDGE,"E38.3.1")])],"isStart":false});
            var Q5;
            Q5=makeQuery(id+"F18.opExtrude","CAP_EDGE",EDGE,{"disambiguationData":[OSD([sQuery(id+"F17.wireOp",EDGE,"E38.3.3")])],"isStart":false});
            var Q6;
            Q6=makeQuery(id+"F18.opExtrude","CAP_EDGE",EDGE,{"disambiguationData":[OSD([sQuery(id+"F17.wireOp",EDGE,"E38.2.4")])],"isStart":false});
            var Q7;
            Q7=makeQuery(id+"F18.opExtrude","CAP_EDGE",EDGE,{"disambiguationData":[OSD([sQuery(id+"F17.wireOp",EDGE,"E38.2.3")])],"isStart":false});
            var Q8;
            Q8=makeQuery(id+"F18.opExtrude","CAP_EDGE",EDGE,{"disambiguationData":[OSD([sQuery(id+"F17.wireOp",EDGE,"E38.1.5"),sQuery(id+"F17.wireOp",EDGE,"E38.2.1")])],"isStart":false});
            var Q9;
            Q9=makeQuery(id+"F18.opExtrude","CAP_EDGE",EDGE,{"disambiguationData":[OSD([sQuery(id+"F17.wireOp",EDGE,"E38.1.4")])],"isStart":false});
            var Q10;
            Q10=makeQuery(id+"F18.opExtrude","CAP_EDGE",EDGE,{"disambiguationData":[OSD([sQuery(id+"F17.wireOp",EDGE,"E38.1.3")])],"isStart":false});
            var Q11;
            Q11=makeQuery(id+"F18.opExtrude","CAP_EDGE",EDGE,{"disambiguationData":[OSD([sQuery(id+"F17.wireOp",EDGE,"E35"),sQuery(id+"F17.wireOp",EDGE,"E38.1.1")])],"isStart":false});
            var Q12;
            Q12=makeQuery(id+"F18.opExtrude","CAP_EDGE",EDGE,{"disambiguationData":[OSD([sQuery(id+"F17.wireOp",EDGE,"E34")])],"isStart":false});
            var Q13;
            Q13=makeQuery(id+"F18.opExtrude","CAP_EDGE",EDGE,{"disambiguationData":[OSD([sQuery(id+"F17.wireOp",EDGE,"E33")])],"isStart":false});
            chamfer(context, id + "F23", {"entities" : qUnion([Q0, Q1, Q2, Q3, Q4, Q5, Q6, Q7, Q8, Q9, Q10, Q11, Q12, Q13]), "width" : .8 * mm, "tangentPropagation" : true});
        }
        {
            var Q0;
            Q0=makeQuery(id+"F16.opExtrude","CAP_FACE",FACE,{"disambiguationData":[OSD([sQuery(id+"F15.wireOp",EDGE,"E27"),sQuery(id+"F15.wireOp",EDGE,"E28"),sQuery(id+"F15.wireOp",EDGE,"E29"),sQuery(id+"F15.wireOp",EDGE,"E30")])],"isStart":false});
            var sketch = newSketch(context, id + "F24", { "sketchPlane" : qUnion([Q0])});
            skArc(sketch, "E47", {"start": v(6.62, 11.19) * mm, "mid": v(-13, 0) * mm, "end": v(6.62, -11.19) * mm});
            skArc(sketch, "E48", {"start": v(5.7, 9.75) * mm, "mid": v(-11.3, 0) * mm, "end": v(5.7, -9.75) * mm});
            skArc(sketch, "E49", {"start": v(5.7, 9.75) * mm, "mid": v(6.82, 10.05) * mm, "end": v(6.62, 11.19) * mm});
            skArc(sketch, "E50.MirrorCS", {"start": v(5.7, -9.75) * mm, "mid": v(6.82, -10.05) * mm, "end": v(6.62, -11.19) * mm});
            skSolve(sketch);
        }
        {
            var Q0;
            Q0 = qSketchRegion(id + "F24", true);
            extrude(context, id + "F25", {"entities" : qUnion([Q0]), "operationType" : NewBodyOperationType.ADD, "depth" : 3 * mm, "offsetDistance" : 25 * mm});
        }
        {
            var Q0;
            Q0=makeQuery(id+"F22.opExtrude","CAP_FACE",FACE,{"disambiguationData":[OSD([sQuery(id+"F21.wireOp",EDGE,"E46")])],"isStart":false});
            var sketch = newSketch(context, id + "F26", { "sketchPlane" : qUnion([Q0])});
            skLineSegment(sketch, "E51", {"start": v(23.6, 1.4) * mm, "end": v(24.1, 1.83) * mm});
            skLineSegment(sketch, "E52.MirrorCS", {"start": v(23.6, 1.4) * mm, "end": v(24.1, 0.97) * mm});
            skLineSegment(sketch, "E53.1.0", {"start": v(23.5, 2.12) * mm, "end": v(23.88, 2.67) * mm});
            skLineSegment(sketch, "E53.1.1", {"start": v(23.5, 2.12) * mm, "end": v(24.1, 1.83) * mm});
            skLineSegment(sketch, "E53.2.0", {"start": v(23.22, 2.8) * mm, "end": v(23.44, 3.43) * mm});
            skLineSegment(sketch, "E53.2.1", {"start": v(23.22, 2.8) * mm, "end": v(23.88, 2.67) * mm});
            skLineSegment(sketch, "E53.3.0", {"start": v(22.78, 3.38) * mm, "end": v(22.83, 4.04) * mm});
            skLineSegment(sketch, "E53.3.1", {"start": v(22.78, 3.38) * mm, "end": v(23.44, 3.43) * mm});
            skLineSegment(sketch, "E53.4.0", {"start": v(22.2, 3.82) * mm, "end": v(22.07, 4.48) * mm});
            skLineSegment(sketch, "E53.4.1", {"start": v(22.2, 3.82) * mm, "end": v(22.83, 4.04) * mm});
            skLineSegment(sketch, "E53.5.0", {"start": v(21.52, 4.1) * mm, "end": v(21.23, 4.7) * mm});
            skLineSegment(sketch, "E53.5.1", {"start": v(21.52, 4.1) * mm, "end": v(22.07, 4.48) * mm});
            skLineSegment(sketch, "E53.6.0", {"start": v(20.8, 4.2) * mm, "end": v(20.37, 4.7) * mm});
            skLineSegment(sketch, "E53.6.1", {"start": v(20.8, 4.2) * mm, "end": v(21.23, 4.7) * mm});
            skLineSegment(sketch, "E53.7.0", {"start": v(20.08, 4.1) * mm, "end": v(19.53, 4.48) * mm});
            skLineSegment(sketch, "E53.7.1", {"start": v(20.08, 4.1) * mm, "end": v(20.37, 4.7) * mm});
            skLineSegment(sketch, "E53.8.0", {"start": v(19.4, 3.82) * mm, "end": v(18.77, 4.04) * mm});
            skLineSegment(sketch, "E53.8.1", {"start": v(19.4, 3.82) * mm, "end": v(19.53, 4.48) * mm});
            skLineSegment(sketch, "E53.9.0", {"start": v(18.82, 3.38) * mm, "end": v(18.16, 3.43) * mm});
            skLineSegment(sketch, "E53.9.1", {"start": v(18.82, 3.38) * mm, "end": v(18.77, 4.04) * mm});
            skLineSegment(sketch, "E53.10.0", {"start": v(18.38, 2.8) * mm, "end": v(17.72, 2.67) * mm});
            skLineSegment(sketch, "E53.10.1", {"start": v(18.38, 2.8) * mm, "end": v(18.16, 3.43) * mm});
            skLineSegment(sketch, "E53.11.0", {"start": v(18.1, 2.12) * mm, "end": v(17.5, 1.83) * mm});
            skLineSegment(sketch, "E53.11.1", {"start": v(18.1, 2.12) * mm, "end": v(17.72, 2.67) * mm});
            skLineSegment(sketch, "E53.12.0", {"start": v(18, 1.4) * mm, "end": v(17.5, 0.97) * mm});
            skLineSegment(sketch, "E53.12.1", {"start": v(18, 1.4) * mm, "end": v(17.5, 1.83) * mm});
            skLineSegment(sketch, "E53.13.0", {"start": v(18.1, 0.68) * mm, "end": v(17.72, 0.13) * mm});
            skLineSegment(sketch, "E53.13.1", {"start": v(18.1, 0.68) * mm, "end": v(17.5, 0.97) * mm});
            skLineSegment(sketch, "E53.14.0", {"start": v(18.38, 0) * mm, "end": v(18.16, -0.63) * mm});
            skLineSegment(sketch, "E53.14.1", {"start": v(18.38, 0) * mm, "end": v(17.72, 0.13) * mm});
            skPoint(sketch, "E53.center", {"position": v(20.8, 1.4) * mm});
            skLineSegment(sketch, "E54.1.15.0", {"start": v(18.82, -0.58) * mm, "end": v(18.77, -1.24) * mm});
            skLineSegment(sketch, "E54.3.15.0", {"start": v(18.82, -0.58) * mm, "end": v(18.16, -0.63) * mm});
            skLineSegment(sketch, "E54.1.16.0", {"start": v(19.4, -1.02) * mm, "end": v(19.53, -1.68) * mm});
            skLineSegment(sketch, "E54.3.16.0", {"start": v(19.4, -1.02) * mm, "end": v(18.77, -1.24) * mm});
            skLineSegment(sketch, "E54.1.17.0", {"start": v(20.08, -1.3) * mm, "end": v(20.37, -1.9) * mm});
            skLineSegment(sketch, "E54.3.17.0", {"start": v(20.08, -1.3) * mm, "end": v(19.53, -1.68) * mm});
            skLineSegment(sketch, "E54.1.18.0", {"start": v(20.8, -1.4) * mm, "end": v(21.23, -1.9) * mm});
            skLineSegment(sketch, "E54.3.18.0", {"start": v(20.8, -1.4) * mm, "end": v(20.37, -1.9) * mm});
            skLineSegment(sketch, "E54.1.19.0", {"start": v(21.52, -1.3) * mm, "end": v(22.07, -1.68) * mm});
            skLineSegment(sketch, "E54.3.19.0", {"start": v(21.52, -1.3) * mm, "end": v(21.23, -1.9) * mm});
            skLineSegment(sketch, "E54.1.20.0", {"start": v(22.2, -1.02) * mm, "end": v(22.83, -1.24) * mm});
            skLineSegment(sketch, "E54.3.20.0", {"start": v(22.2, -1.02) * mm, "end": v(22.07, -1.68) * mm});
            skLineSegment(sketch, "E54.1.21.0", {"start": v(22.78, -0.58) * mm, "end": v(23.44, -0.63) * mm});
            skLineSegment(sketch, "E54.3.21.0", {"start": v(22.78, -0.58) * mm, "end": v(22.83, -1.24) * mm});
            skLineSegment(sketch, "E54.1.22.0", {"start": v(23.22, 0) * mm, "end": v(23.88, 0.13) * mm});
            skLineSegment(sketch, "E54.3.22.0", {"start": v(23.22, 0) * mm, "end": v(23.44, -0.63) * mm});
            skLineSegment(sketch, "E54.1.23.0", {"start": v(23.5, 0.68) * mm, "end": v(24.1, 0.97) * mm});
            skLineSegment(sketch, "E54.3.23.0", {"start": v(23.5, 0.68) * mm, "end": v(23.88, 0.13) * mm});
            skSolve(sketch);
        }
        {
            var Q0;
            Q0 = qSketchRegion(id + "F26", true);
            extrude(context, id + "F27", {"entities" : qUnion([Q0]), "operationType" : NewBodyOperationType.REMOVE, "oppositeDirection" : true, "depth" : 5 * mm, "offsetDistance" : 25 * mm});
        }
        {
            var Q0;
            Q0=makeQuery(id+"F27.boolean.opBoolean","COPY",FACE,{"derivedFrom":makeQuery(id+"F27.opExtrude","CAP_FACE",FACE,{"disambiguationData":[OSD([sQuery(id+"F26.wireOp",EDGE,"E51"),sQuery(id+"F26.wireOp",EDGE,"E52.MirrorCS"),sQuery(id+"F26.wireOp",EDGE,"E53.1.0"),sQuery(id+"F26.wireOp",EDGE,"E53.1.1"),sQuery(id+"F26.wireOp",EDGE,"E53.2.0"),sQuery(id+"F26.wireOp",EDGE,"E53.2.1"),sQuery(id+"F26.wireOp",EDGE,"E53.3.0"),sQuery(id+"F26.wireOp",EDGE,"E53.3.1"),sQuery(id+"F26.wireOp",EDGE,"E53.4.0"),sQuery(id+"F26.wireOp",EDGE,"E53.4.1"),sQuery(id+"F26.wireOp",EDGE,"E53.5.0"),sQuery(id+"F26.wireOp",EDGE,"E53.5.1"),sQuery(id+"F26.wireOp",EDGE,"E53.6.0"),sQuery(id+"F26.wireOp",EDGE,"E53.6.1"),sQuery(id+"F26.wireOp",EDGE,"E53.7.0"),sQuery(id+"F26.wireOp",EDGE,"E53.7.1"),sQuery(id+"F26.wireOp",EDGE,"E53.8.0"),sQuery(id+"F26.wireOp",EDGE,"E53.8.1"),sQuery(id+"F26.wireOp",EDGE,"E53.9.0"),sQuery(id+"F26.wireOp",EDGE,"E53.9.1"),sQuery(id+"F26.wireOp",EDGE,"E53.10.0"),sQuery(id+"F26.wireOp",EDGE,"E53.10.1"),sQuery(id+"F26.wireOp",EDGE,"E53.11.0"),sQuery(id+"F26.wireOp",EDGE,"E53.11.1"),sQuery(id+"F26.wireOp",EDGE,"E53.12.0"),sQuery(id+"F26.wireOp",EDGE,"E53.12.1"),sQuery(id+"F26.wireOp",EDGE,"E53.13.0"),sQuery(id+"F26.wireOp",EDGE,"E53.13.1"),sQuery(id+"F26.wireOp",EDGE,"E53.14.0"),sQuery(id+"F26.wireOp",EDGE,"E53.14.1"),sQuery(id+"F26.wireOp",EDGE,"E54.1.15.0"),sQuery(id+"F26.wireOp",EDGE,"E54.3.15.0"),sQuery(id+"F26.wireOp",EDGE,"E54.1.16.0"),sQuery(id+"F26.wireOp",EDGE,"E54.3.16.0"),sQuery(id+"F26.wireOp",EDGE,"E54.1.17.0"),sQuery(id+"F26.wireOp",EDGE,"E54.3.17.0"),sQuery(id+"F26.wireOp",EDGE,"E54.1.18.0"),sQuery(id+"F26.wireOp",EDGE,"E54.3.18.0"),sQuery(id+"F26.wireOp",EDGE,"E54.1.19.0"),sQuery(id+"F26.wireOp",EDGE,"E54.3.19.0"),sQuery(id+"F26.wireOp",EDGE,"E54.1.20.0"),sQuery(id+"F26.wireOp",EDGE,"E54.3.20.0"),sQuery(id+"F26.wireOp",EDGE,"E54.1.21.0"),sQuery(id+"F26.wireOp",EDGE,"E54.3.21.0"),sQuery(id+"F26.wireOp",EDGE,"E54.1.22.0"),sQuery(id+"F26.wireOp",EDGE,"E54.3.22.0"),sQuery(id+"F26.wireOp",EDGE,"E54.1.23.0"),sQuery(id+"F26.wireOp",EDGE,"E54.3.23.0")])],"isStart":false})});
            chamfer(context, id + "F28", {"entities" : qUnion([Q0]), "width" : 1 * mm, "tangentPropagation" : true});
        }
    });
